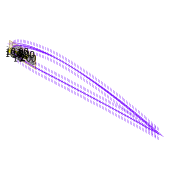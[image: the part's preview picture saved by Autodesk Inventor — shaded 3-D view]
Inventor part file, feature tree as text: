
AUTODESK INVENTOR PART (.ipt)
format: ipt  version: 2022 (Build 260153000, 153)  size: 433,152 bytes
history: native  units: mm
features: extrude x7, sketch x6, projected_geometry x3, plane x2, fillet x2, shell x1
ambient origin geometry x8: Origin, YZ Plane, XZ Plane, XY Plane, X Axis, Y Axis, Z Axis, Center Point
bodies: Solid1 (feature_tree)
feature tree (21):
  extrude  "Extrusion1"  Depth=3.0mm
  shell  "Shell1"  Thickness=6.454mm
  plane  "Work Plane3"
  extrude  "Extrusion10"  Depth=12.0mm
  fillet  "Fillet2"  Radius=18.0mm
  fillet  "Fillet3"  Radius=13.0mm
  extrude  "Extrusion16"  Depth=5.0mm
  extrude  "Extrusion17"  Depth=1.5mm
  extrude  "Extrusion11"  Depth=1.0mm
  plane  "Work Plane4"
  sketch  "Sketch44"  dims[d86=2.7mm d87=4.0mm d88=4.0mm d89=20.0mm d90=0.0mm d93=-8.0mm d97=2.0mm d159=15.0mm d160=5.0mm d161=8.0mm d162=0.0mm d163=30.0mm d164=100.0mm d165=0.0mm d184=1.745329mm d185=1.745329mm d186=1.745329mm d187=1.745329mm d188=2.0mm d189=2.0mm d190=2.0mm d191=2.0mm d192=10.0mm d193=0.0mm d194=8.0mm d195=0.0mm d168=0.5mm d169=0.872665mm d170=0.5mm d171=0.872665mm]
  extrude  "Extrusion22"  Depth=10.0mm
  extrude  "Extrusion23"  Depth=10.0mm
  sketch  "Sketch3"  dims[d0=8.0mm d1=0.0mm d2=3.0mm d74=6.454mm]
  sketch  "Sketch29"  dims[d75=63.621mm d76=12.0mm d77=18.0mm d78=13.0mm]
  projected_geometry  "Projected Loop14"
  sketch  "Sketch31"  dims[d79=13.0mm d80=5.0mm]
  sketch  "Sketch37"  dims[d81=1.5mm d82=1.5mm]
  projected_geometry  "Projected Loop20"
  sketch  "Sketch38"  dims[d83=8.0mm d84=0.0mm d85=1.0mm]
  projected_geometry  "Projected Loop21"
